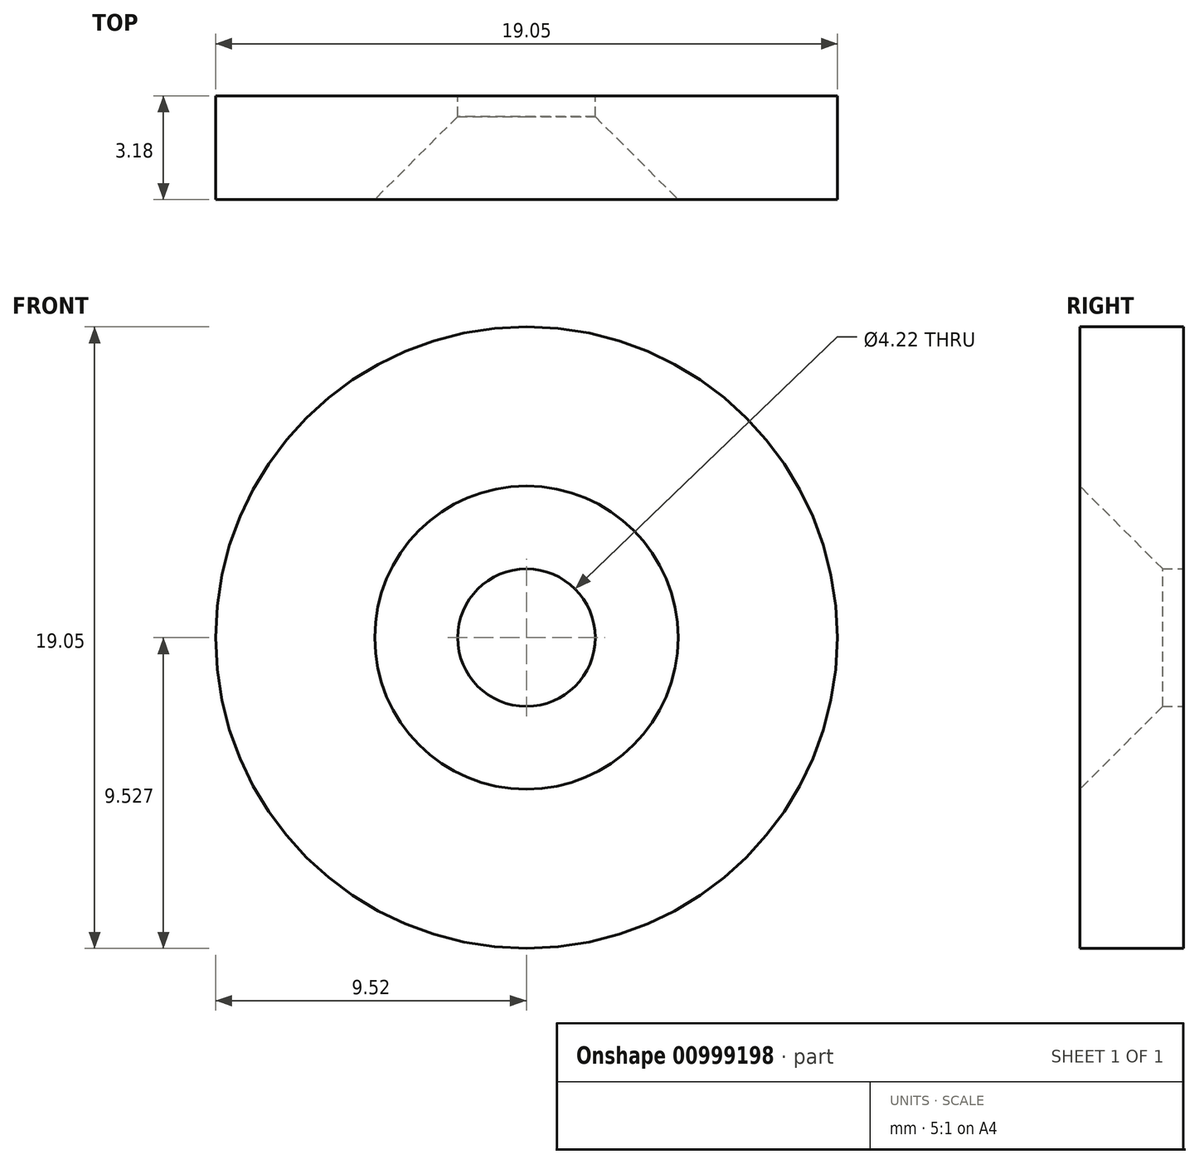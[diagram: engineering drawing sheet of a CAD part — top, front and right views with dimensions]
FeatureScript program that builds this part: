
annotation { "Feature Type Name" : "Feature", "Feature Type Description" : "" }
export const myFeature = defineFeature(function(context is Context, id is Id, definition is map)
    precondition{}
    {
        {
            var Q0;
            Q0=qCreatedBy(makeId("Front.planeOp"),FACE);
            var sketch = newSketch(context, id + "F0", { "sketchPlane" : qUnion([Q0])});
            skCircle(sketch, "E0", {"center": v(16.58, 21.12) * mm, "radius": 9.53 * mm});
            skCircle(sketch, "E1", {"center": v(16.58, 21.12) * mm, "radius": 2.1 * mm});
            skSolve(sketch);
        }
        {
            var Q0;
            Q0 = qSketchRegion(id + "F0", true);
            extrude(context, id + "F1", {"entities" : qUnion([Q0]), "depth" : 3.17 * mm, "offsetDistance" : 25.4 * mm});
        }
        {
            var Q0;
            Q0=makeQuery(id+"F1.opExtrude","CAP_EDGE",EDGE,{"disambiguationData":[OSD([sQuery(id+"F0.wireOp",EDGE,"E1")])],"isStart":false});
            chamfer(context, id + "F2", {"entities" : qUnion([Q0]), "width" : 2.54 * mm, "tangentPropagation" : true});
        }
    });
